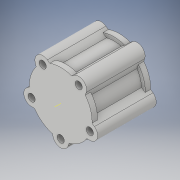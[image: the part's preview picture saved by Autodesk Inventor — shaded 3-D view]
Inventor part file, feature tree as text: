
AUTODESK INVENTOR PART (.ipt)
format: ipt  version: 2018 (Build 220112000, 112)  size: 207,360 bytes
history: native  units: in
note: dims shown in document units (in); Inventor stores cm internally (conversion verified against a paired STEP export)
features: extrude x5, sketch x5, pattern_circular x2, shell x1, other x1, projected_geometry x1
ambient origin geometry x8: Origin, YZ Plane, XZ Plane, XY Plane, X Axis, Y Axis, Z Axis, Center Point
bodies: Solid1 (feature_tree)
feature tree (15):
  extrude  "Extrusion1"  Depth=6.3976in TaperAngle=0.0deg
  shell  "Shell1"  Thickness=0.2362in
  extrude  "Extrusion2"  Depth=6.063in
  extrude  "Extrusion3"  Depth=0.5906in TaperAngle=0.0deg
  extrude  "Extrusion4"  Depth=3.3465in
  other  "Work Axis1"
  pattern_circular  "Circular Pattern1"  Count=5 Angle=360.0deg
  extrude  "Extrusion5"  Depth=6.3976in TaperAngle=360.0deg
  pattern_circular  "Circular Pattern2"  Count=2  [1 undecoded]
  sketch  "Sketch1"  dims[d0=6.063in d1=6.3976in d2=0.0in d3=0.2362in]
  sketch  "Sketch2"  dims[d4=6.8504in d5=6.063in]
  sketch  "Sketch3"  dims[d6=0.5906in d7=0.0in d8=0.5906in d9=0.0in]
  sketch  "Sketch4"  dims[d11=3.3465in d12=0.2474in]
  projected_geometry  "Projected Loop1"
  sketch  "Sketch5"  dims[d13=6.3976in d14=0.0in d15=1.9685in d17=360.0deg d19=1.9685in d20=360.0deg d22=0.7874in d23=6.3976in d24=0.0in d25=1.9685in d26=360.0deg]
note: 1 required parameter value undecoded (feature->parameter linkage not recoverable at this tier; creation-order binding heuristic only, values carry confidence <= 0.55)
